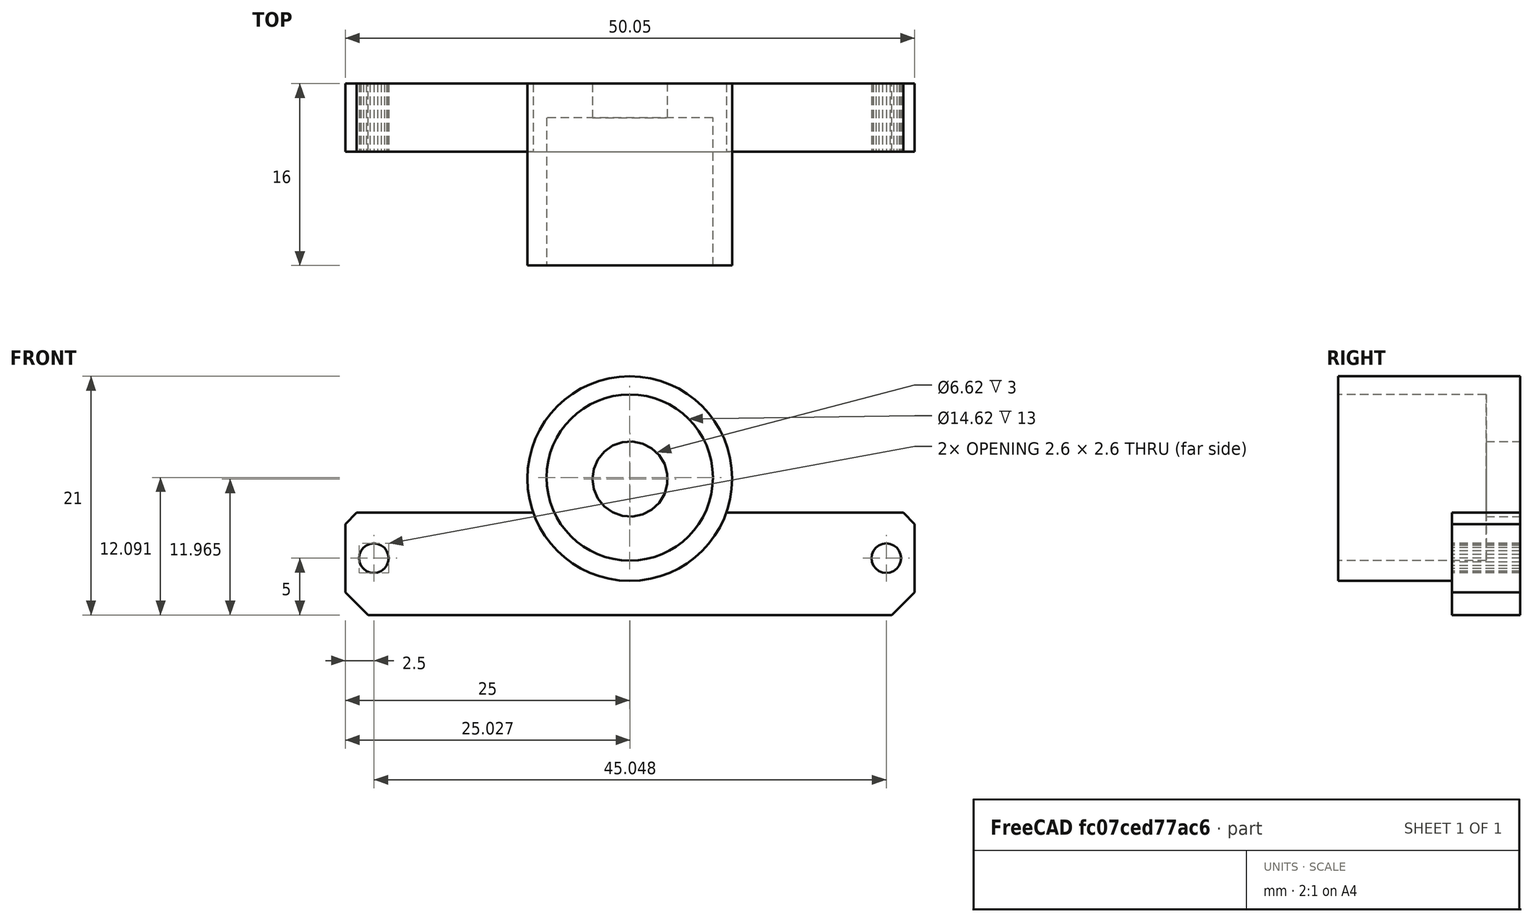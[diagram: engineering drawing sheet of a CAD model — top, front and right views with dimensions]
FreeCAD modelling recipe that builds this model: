
FCSTD DOCUMENT  (FreeCAD 0.19R24267 +148 (Git))
Label: XYstage_MicroLid
License: All rights reserved
LicenseURL: http://en.wikipedia.org/wiki/All_rights_reserved
objects: PartDesign::FeatureBase×3, PartDesign::Body×3, Sketcher::SketchObject×2, PartDesign::Pocket×2, Part::Feature×1, Part::Cylinder×1, Part::MultiFuse×1, Part::Refine×1
note: 16 computed .brp shape members not serialized (recipe doc carries the construction recipe); baked Part::Feature solids carry a one-line shape summary decoded from their .brp

FEATURE [Part::Feature] LinearRailTest_MicroLid_test001001_solid  label="LinearRailTest_MicroLid_test001001 (Solid)"
  shape: bbox 50.05 x 6 x 17 mm, 120 faces (baked)
FEATURE [Part::Cylinder] Cylinder
  Angle = 360
  AttacherType = Attacher::AttachEngine3D
  Height = 16
  Placement = pos=(0,0,0) rot=(1,0,0;1.5708rad)
  Radius = 9
FEATURE [PartDesign::FeatureBase] BaseFeature
  BaseFeature = -> Cylinder
FEATURE [PartDesign::Body] Body
  BaseFeature = -> Cylinder
  Group = -> [BaseFeature]
  Origin = -> Origin
  Placement = pos=(0,9e-16,-16) rot=(1,0,0;1.5708rad)
  Tip = -> BaseFeature
FEATURE [Part::MultiFuse] Fusion
  Shapes = -> [Body,LinearRailTest_MicroLid_test001001_solid]
FEATURE [PartDesign::FeatureBase] BaseFeature001
  BaseFeature = -> Fusion
FEATURE [PartDesign::Body] Body001
  BaseFeature = -> Fusion
  Group = -> [BaseFeature001]
  Origin = -> Origin001
  Tip = -> BaseFeature001
FEATURE [Part::Refine] Body001001
  Source = -> Body001
FEATURE [PartDesign::FeatureBase] BaseFeature002
  BaseFeature = -> Body001001
FEATURE [Sketcher::SketchObject] Sketch
  FullyConstrained = false
  MapMode = 5
  Placement = pos=(0,-16,-3.6e-15) rot=(1,0,0;1.5708rad)
  Support = -> [BaseFeature002]
  sketch-geometry (3):
    g0: GeomPoint X=0 Y=-25.0041 Z=0
    g1: GeomPoint X=0 Y=-7.01493 Z=0
    g2: Circle CenterX=0 CenterY=-15.9087 CenterZ=0 NormalX=0 NormalY=0 NormalZ=1 AngleXU=0 Radius=7.31228
  constraints (3):
    c: PointOnObject(g0,g-2)
    c: PointOnObject(g1,g-2)
    c: PointOnObject(g2,g-2)
FEATURE [PartDesign::Pocket] Pocket
  BaseFeature = -> BaseFeature002
  Length = 13
  Length2 = 100
  Profile = -> Sketch
  Type = 0
FEATURE [Sketcher::SketchObject] Sketch001
  FullyConstrained = false
  MapMode = 5
  Placement = pos=(0,-2.59445e-08,0) rot=(0,0.707107,0.707107;3.14159rad)
  Support = -> [Pocket]
  sketch-geometry (1):
    g0: Circle CenterX=-0.026626 CenterY=-16.035 CenterZ=0 NormalX=0 NormalY=0 NormalZ=1 AngleXU=0 Radius=3.3078
FEATURE [PartDesign::Pocket] Pocket001
  BaseFeature = -> Pocket
  Length = 5
  Length2 = 100
  Profile = -> Sketch001
  Type = 0
FEATURE [PartDesign::Body] Body001002
  BaseFeature = -> Body001001
  Group = -> [BaseFeature002,Sketch,Pocket,Sketch001,Pocket001]
  Origin = -> Origin002
  Tip = -> Pocket001
